AUTODESK INVENTOR PART (.ipt)
format: ipt  version: 2015 SP1 (Build 190203100, 203)  size: 222,208 bytes
history: native  units: in
note: dims shown in document units (in); Inventor stores cm internally (conversion verified against a paired STEP export)
features: sketch x4, extrude x3, fillet x2, reference x2, hole x1
ambient origin geometry x8: Origin, YZ Plane, XZ Plane, XY Plane, X Axis, Y Axis, Z Axis, Center Point
bodies: Solid1 (feature_tree)
feature tree (12):
  extrude  "Extrusion1"  Depth=8.0in
  extrude  "Extrusion2"  Depth=0.125in
  fillet  "Fillet1"  Radius=1.0in
  hole  "Hole1"  [1 undecoded]
  extrude  "Extrusion3"  Depth=1.25in
  fillet  "Fillet2"  Radius=2.0in
  sketch  "Sketch1"  dims[d0=6.0in d1=8.0in]
  sketch  "Sketch2"  dims[d2=0.125in d3=0.0in d4=8.46in d5=1.0in d6=0.0in]
  sketch  "Sketch3"  dims[d7=0.5in]
  reference  "Reference1"
  reference  "Reference2"
  sketch  "Sketch4"  dims[d8=0.163in d9=0.75in d10=0.375in d11=0.25in d12=0.5635in d13=1.0in d14=0.8108in d15=1.1811in d17=0.5in d18=0.3937in d20=1.0in d23=1.25in d24=2.0in d25=3.0in d26=1.0in d27=0.0in d28=0.5in]
note: 1 required parameter value undecoded (feature->parameter linkage not recoverable at this tier; creation-order binding heuristic only, values carry confidence <= 0.55)
